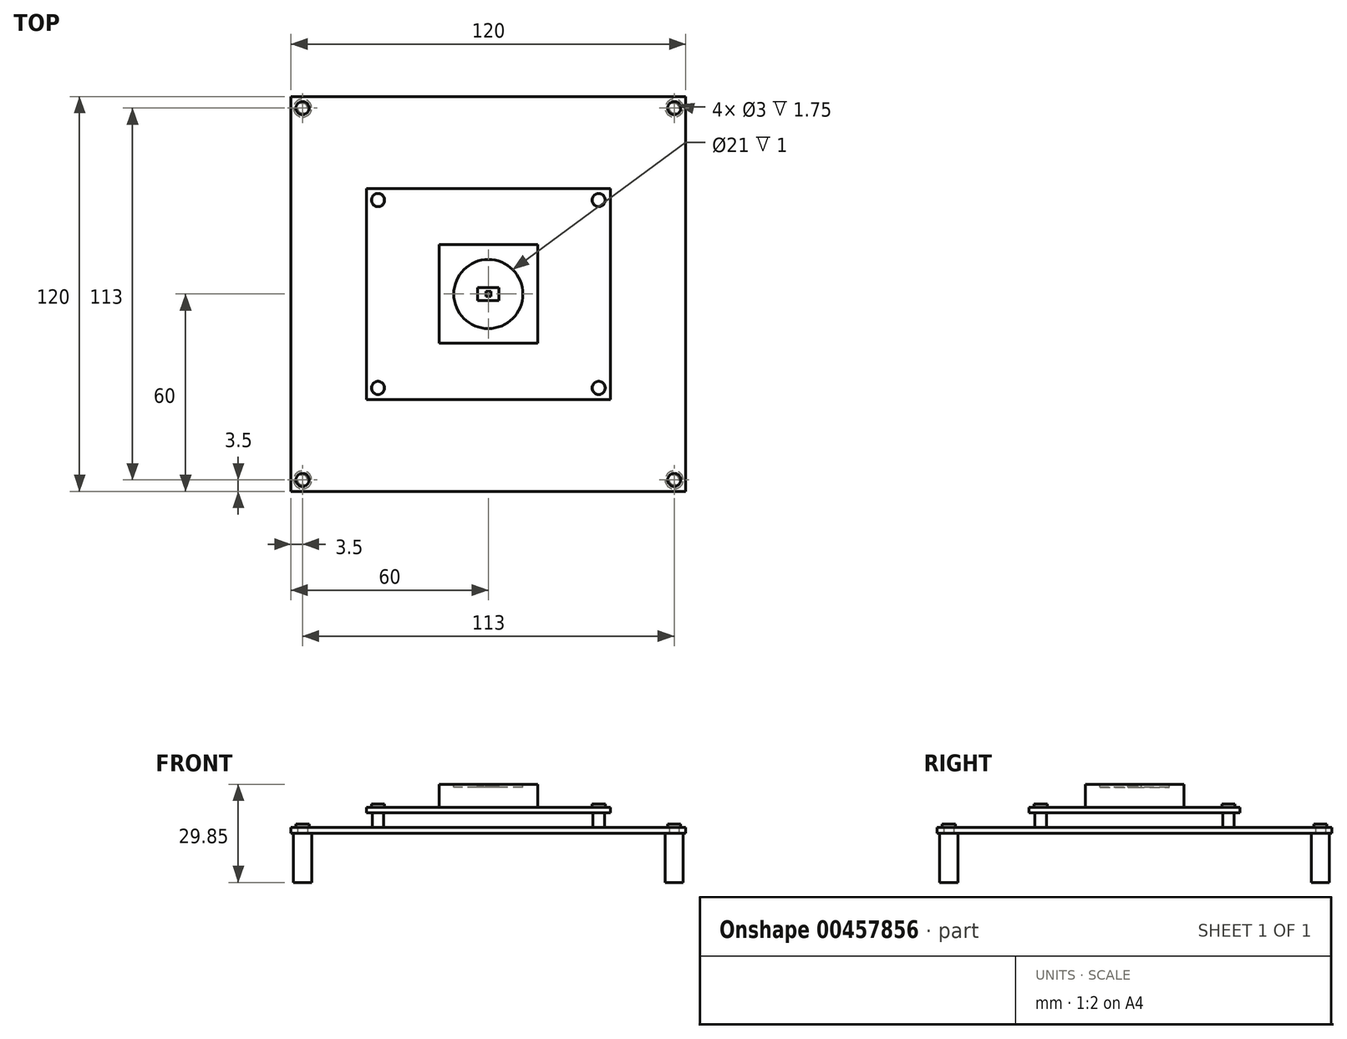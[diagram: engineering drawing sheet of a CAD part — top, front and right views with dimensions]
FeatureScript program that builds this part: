
annotation { "Feature Type Name" : "Feature", "Feature Type Description" : "" }
export const myFeature = defineFeature(function(context is Context, id is Id, definition is map)
    precondition{}
    {
        {
            var Q0;
            Q0=qCreatedBy(makeId("Top.planeOp"),FACE);
            var sketch = newSketch(context, id + "F0", { "sketchPlane" : qUnion([Q0])});
            skLineSegment(sketch, "E0.bottom", {"start": v(60, -60) * mm, "end": v(-60, -60) * mm});
            skLineSegment(sketch, "E0.top", {"start": v(60, 60) * mm, "end": v(-60, 60) * mm});
            skLineSegment(sketch, "E0.left", {"start": v(60, -60) * mm, "end": v(60, 60) * mm});
            skLineSegment(sketch, "E0.right", {"start": v(-60, -60) * mm, "end": v(-60, 60) * mm});
            skPoint(sketch, "E0.middle", {"position": v(0, 0) * mm});
            skCircle(sketch, "E1", {"center": v(-56.5, 56.5) * mm, "radius": 1.5 * mm});
            skCircle(sketch, "E2", {"center": v(56.5, 56.5) * mm, "radius": 1.5 * mm});
            skCircle(sketch, "E3", {"center": v(-56.5, -56.5) * mm, "radius": 1.5 * mm});
            skCircle(sketch, "E4", {"center": v(56.5, -56.5) * mm, "radius": 1.5 * mm});
            skCircle(sketch, "E5", {"center": v(-56.5, 56.5) * mm, "radius": 1.5 * mm, "construction": true});
            skCircle(sketch, "E6", {"center": v(-56.5, -56.5) * mm, "radius": 1.5 * mm, "construction": true});
            skCircle(sketch, "E7", {"center": v(56.5, -56.5) * mm, "radius": 1.5 * mm, "construction": true});
            skCircle(sketch, "E8", {"center": v(56.5, 56.5) * mm, "radius": 1.5 * mm, "construction": true});
            skCircle(sketch, "E9", {"center": v(-33.55, 28.55) * mm, "radius": 1.5 * mm, "construction": true});
            skCircle(sketch, "E10", {"center": v(33.55, 28.55) * mm, "radius": 1.5 * mm, "construction": true});
            skCircle(sketch, "E11", {"center": v(-33.55, -28.55) * mm, "radius": 1.5 * mm, "construction": true});
            skCircle(sketch, "E12", {"center": v(33.55, -28.55) * mm, "radius": 1.5 * mm, "construction": true});
            skLineSegment(sketch, "E13", {"start": v(-33.55, 28.55) * mm, "end": v(33.55, -28.55) * mm, "construction": true});
            skLineSegment(sketch, "E14", {"start": v(33.55, 28.55) * mm, "end": v(-33.55, -28.55) * mm, "construction": true});
            skLineSegment(sketch, "E15.bottom", {"start": v(37.05, 32.05) * mm, "end": v(-37.05, 32.05) * mm, "construction": true});
            skLineSegment(sketch, "E15.top", {"start": v(37.05, -32.05) * mm, "end": v(-37.05, -32.05) * mm, "construction": true});
            skLineSegment(sketch, "E15.left", {"start": v(37.05, 32.05) * mm, "end": v(37.05, -32.05) * mm, "construction": true});
            skLineSegment(sketch, "E15.right", {"start": v(-37.05, 32.05) * mm, "end": v(-37.05, -32.05) * mm, "construction": true});
            skLineSegment(sketch, "E16.bottom", {"start": v(15, -15) * mm, "end": v(-15, -15) * mm, "construction": true});
            skLineSegment(sketch, "E16.top", {"start": v(15, 15) * mm, "end": v(-15, 15) * mm, "construction": true});
            skLineSegment(sketch, "E16.left", {"start": v(15, -15) * mm, "end": v(15, 15) * mm, "construction": true});
            skLineSegment(sketch, "E16.right", {"start": v(-15, -15) * mm, "end": v(-15, 15) * mm, "construction": true});
            skSolve(sketch);
        }
        {
            var Q0;
            Q0=makeQuery(id+"F0.imprint","IMPRINT",FACE,{"disambiguationData":[TD([[makeQuery(id+"F0.imprint","IMPRINT",EDGE,{"derivedFrom":sQuery(id+"F0.wireOp",EDGE,"E0.bottom")}),-1.0]])]});
            extrude(context, id + "F1", {"entities" : qUnion([Q0]), "depth" : 1.75 * mm});
        }
        {
            var Q0;
            Q0=makeQuery(id+"F1.opExtrude","CAP_FACE",FACE,{"disambiguationData":[OSD([sQuery(id+"F0.wireOp",EDGE,"E0.bottom"),sQuery(id+"F0.wireOp",EDGE,"E0.top"),sQuery(id+"F0.wireOp",EDGE,"E0.left"),sQuery(id+"F0.wireOp",EDGE,"E0.right"),sQuery(id+"F0.wireOp",EDGE,"E1"),sQuery(id+"F0.wireOp",EDGE,"E2"),sQuery(id+"F0.wireOp",EDGE,"E3"),sQuery(id+"F0.wireOp",EDGE,"E4")])],"isStart":true});
            var sketch = newSketch(context, id + "F2", { "sketchPlane" : qUnion([Q0])});
            skCircle(sketch, "E17", {"center": v(56.5, -56.5) * mm, "radius": 2.75 * mm});
            skCircle(sketch, "E18", {"center": v(-56.5, -56.5) * mm, "radius": 2.75 * mm});
            skCircle(sketch, "E19", {"center": v(-56.5, 56.5) * mm, "radius": 2.75 * mm});
            skCircle(sketch, "E20", {"center": v(56.5, 56.5) * mm, "radius": 2.75 * mm});
            skSolve(sketch);
        }
        {
            var Q0;
            Q0=makeQuery(id+"F2.imprint","IMPRINT",FACE,{"disambiguationData":[TD([[makeQuery(id+"F2.imprint","IMPRINT",EDGE,{"derivedFrom":sQuery(id+"F2.wireOp",EDGE,"E19")}),1.0]])]});
            var Q1;
            Q1=makeQuery(id+"F2.imprint","IMPRINT",FACE,{"disambiguationData":[TD([[makeQuery(id+"F2.imprint","IMPRINT",EDGE,{"derivedFrom":makeQuery(id+"F1.opExtrude","CAP_EDGE",EDGE,{"disambiguationData":[OSD([sQuery(id+"F0.wireOp",EDGE,"E3")])],"isStart":true})}),-1.0]])]});
            var Q2;
            Q2=makeQuery(id+"F2.imprint","IMPRINT",FACE,{"disambiguationData":[TD([[makeQuery(id+"F2.imprint","IMPRINT",EDGE,{"derivedFrom":makeQuery(id+"F1.opExtrude","CAP_EDGE",EDGE,{"disambiguationData":[OSD([sQuery(id+"F0.wireOp",EDGE,"E4")])],"isStart":true})}),-1.0]])]});
            var Q3;
            Q3=makeQuery(id+"F2.imprint","IMPRINT",FACE,{"disambiguationData":[TD([[makeQuery(id+"F2.imprint","IMPRINT",EDGE,{"derivedFrom":sQuery(id+"F2.wireOp",EDGE,"E20")}),1.0]])]});
            var Q4;
            Q4=makeQuery(id+"F2.imprint","IMPRINT",FACE,{"disambiguationData":[TD([[makeQuery(id+"F2.imprint","IMPRINT",EDGE,{"derivedFrom":sQuery(id+"F2.wireOp",EDGE,"E17")}),1.0]])]});
            var Q5;
            Q5=makeQuery(id+"F2.imprint","IMPRINT",FACE,{"disambiguationData":[TD([[makeQuery(id+"F2.imprint","IMPRINT",EDGE,{"derivedFrom":makeQuery(id+"F1.opExtrude","CAP_EDGE",EDGE,{"disambiguationData":[OSD([sQuery(id+"F0.wireOp",EDGE,"E2")])],"isStart":true})}),-1.0]])]});
            var Q6;
            Q6=makeQuery(id+"F2.imprint","IMPRINT",FACE,{"disambiguationData":[TD([[makeQuery(id+"F2.imprint","IMPRINT",EDGE,{"derivedFrom":makeQuery(id+"F1.opExtrude","CAP_EDGE",EDGE,{"disambiguationData":[OSD([sQuery(id+"F0.wireOp",EDGE,"E1")])],"isStart":true})}),-1.0]])]});
            var Q7;
            Q7=makeQuery(id+"F2.imprint","IMPRINT",FACE,{"disambiguationData":[TD([[makeQuery(id+"F2.imprint","IMPRINT",EDGE,{"derivedFrom":sQuery(id+"F2.wireOp",EDGE,"E18")}),1.0]])]});
            extrude(context, id + "F3", {"entities" : qUnion([Q0, Q1, Q2, Q3, Q4, Q5, Q6, Q7]), "operationType" : NewBodyOperationType.ADD, "depth" : 15 * mm});
        }
        {
            var Q0;
            Q0=makeQuery(id+"F1.opExtrude","CAP_FACE",FACE,{"disambiguationData":[OSD([sQuery(id+"F0.wireOp",EDGE,"E0.bottom"),sQuery(id+"F0.wireOp",EDGE,"E0.top"),sQuery(id+"F0.wireOp",EDGE,"E0.left"),sQuery(id+"F0.wireOp",EDGE,"E0.right"),sQuery(id+"F0.wireOp",EDGE,"E1"),sQuery(id+"F0.wireOp",EDGE,"E2"),sQuery(id+"F0.wireOp",EDGE,"E3"),sQuery(id+"F0.wireOp",EDGE,"E4")])],"isStart":false});
            var sketch = newSketch(context, id + "F4", { "sketchPlane" : qUnion([Q0])});
            skCircle(sketch, "E21", {"center": v(-56.5, 56.5) * mm, "radius": 2 * mm});
            skCircle(sketch, "E22", {"center": v(56.5, 56.5) * mm, "radius": 2 * mm});
            skCircle(sketch, "E23", {"center": v(56.5, -56.5) * mm, "radius": 2 * mm});
            skCircle(sketch, "E24", {"center": v(-56.5, -56.5) * mm, "radius": 2 * mm});
            skPoint(sketch, "E25.0", {"position": v(-33.55, -28.55) * mm});
            skPoint(sketch, "E26.0", {"position": v(33.55, -28.55) * mm});
            skPoint(sketch, "E27.0", {"position": v(-33.55, 28.55) * mm});
            skPoint(sketch, "E28.0", {"position": v(33.55, 28.55) * mm});
            skCircle(sketch, "E29", {"center": v(-33.55, 28.55) * mm, "radius": 1.75 * mm});
            skCircle(sketch, "E30", {"center": v(33.55, 28.55) * mm, "radius": 1.75 * mm});
            skCircle(sketch, "E31", {"center": v(-33.55, -28.55) * mm, "radius": 1.75 * mm});
            skCircle(sketch, "E32", {"center": v(33.55, -28.55) * mm, "radius": 1.75 * mm});
            skSolve(sketch);
        }
        {
            var Q0;
            Q0=makeQuery(id+"F4.imprint","IMPRINT",FACE,{"disambiguationData":[TD([[makeQuery(id+"F4.imprint","IMPRINT",EDGE,{"derivedFrom":sQuery(id+"F4.wireOp",EDGE,"E21")}),1.0]])]});
            var Q1;
            Q1=makeQuery(id+"F4.imprint","IMPRINT",FACE,{"disambiguationData":[TD([[makeQuery(id+"F4.imprint","IMPRINT",EDGE,{"derivedFrom":makeQuery(id+"F1.opExtrude","CAP_EDGE",EDGE,{"disambiguationData":[OSD([sQuery(id+"F0.wireOp",EDGE,"E1")])],"isStart":false})}),1.0]])]});
            var Q2;
            Q2=makeQuery(id+"F4.imprint","IMPRINT",FACE,{"disambiguationData":[TD([[makeQuery(id+"F4.imprint","IMPRINT",EDGE,{"derivedFrom":sQuery(id+"F4.wireOp",EDGE,"E22")}),1.0]])]});
            var Q3;
            Q3=makeQuery(id+"F4.imprint","IMPRINT",FACE,{"disambiguationData":[TD([[makeQuery(id+"F4.imprint","IMPRINT",EDGE,{"derivedFrom":makeQuery(id+"F1.opExtrude","CAP_EDGE",EDGE,{"disambiguationData":[OSD([sQuery(id+"F0.wireOp",EDGE,"E2")])],"isStart":false})}),1.0]])]});
            var Q4;
            Q4=makeQuery(id+"F4.imprint","IMPRINT",FACE,{"disambiguationData":[TD([[makeQuery(id+"F4.imprint","IMPRINT",EDGE,{"derivedFrom":sQuery(id+"F4.wireOp",EDGE,"E23")}),1.0]])]});
            var Q5;
            Q5=makeQuery(id+"F4.imprint","IMPRINT",FACE,{"disambiguationData":[TD([[makeQuery(id+"F4.imprint","IMPRINT",EDGE,{"derivedFrom":makeQuery(id+"F1.opExtrude","CAP_EDGE",EDGE,{"disambiguationData":[OSD([sQuery(id+"F0.wireOp",EDGE,"E4")])],"isStart":false})}),1.0]])]});
            var Q6;
            Q6=makeQuery(id+"F4.imprint","IMPRINT",FACE,{"disambiguationData":[TD([[makeQuery(id+"F4.imprint","IMPRINT",EDGE,{"derivedFrom":sQuery(id+"F4.wireOp",EDGE,"E24")}),1.0]])]});
            var Q7;
            Q7=makeQuery(id+"F4.imprint","IMPRINT",FACE,{"disambiguationData":[TD([[makeQuery(id+"F4.imprint","IMPRINT",EDGE,{"derivedFrom":makeQuery(id+"F1.opExtrude","CAP_EDGE",EDGE,{"disambiguationData":[OSD([sQuery(id+"F0.wireOp",EDGE,"E3")])],"isStart":false})}),1.0]])]});
            extrude(context, id + "F5", {"entities" : qUnion([Q0, Q1, Q2, Q3, Q4, Q5, Q6, Q7]), "operationType" : NewBodyOperationType.ADD, "depth" : 1 * mm});
        }
        {
            var Q0;
            Q0=makeQuery(id+"F4.imprint","IMPRINT",FACE,{"disambiguationData":[TD([[makeQuery(id+"F4.imprint","IMPRINT",EDGE,{"derivedFrom":sQuery(id+"F4.wireOp",EDGE,"E31")}),1.0]])]});
            var Q1;
            Q1=makeQuery(id+"F4.imprint","IMPRINT",FACE,{"disambiguationData":[TD([[makeQuery(id+"F4.imprint","IMPRINT",EDGE,{"derivedFrom":sQuery(id+"F4.wireOp",EDGE,"E32")}),1.0]])]});
            var Q2;
            Q2=makeQuery(id+"F4.imprint","IMPRINT",FACE,{"disambiguationData":[TD([[makeQuery(id+"F4.imprint","IMPRINT",EDGE,{"derivedFrom":sQuery(id+"F4.wireOp",EDGE,"E30")}),1.0]])]});
            var Q3;
            Q3=makeQuery(id+"F4.imprint","IMPRINT",FACE,{"disambiguationData":[TD([[makeQuery(id+"F4.imprint","IMPRINT",EDGE,{"derivedFrom":sQuery(id+"F4.wireOp",EDGE,"E29")}),1.0]])]});
            extrude(context, id + "F6", {"entities" : qUnion([Q0, Q1, Q2, Q3]), "operationType" : NewBodyOperationType.ADD, "depth" : 4.35 * mm});
        }
        {
            var Q0;
            Q0=makeQuery(id+"F6.opExtrude","CAP_FACE",FACE,{"disambiguationData":[OSD([sQuery(id+"F4.wireOp",EDGE,"E29")])],"isStart":false});
            var sketch = newSketch(context, id + "F7", { "sketchPlane" : qUnion([Q0])});
            skPoint(sketch, "E33.0", {"position": v(-37.05, 32.05) * mm});
            skPoint(sketch, "E34.0", {"position": v(37.05, -32.05) * mm});
            skLineSegment(sketch, "E35.bottom", {"start": v(-37.05, 32.05) * mm, "end": v(37.05, 32.05) * mm});
            skLineSegment(sketch, "E35.top", {"start": v(-37.05, -32.05) * mm, "end": v(37.05, -32.05) * mm});
            skLineSegment(sketch, "E35.left", {"start": v(-37.05, 32.05) * mm, "end": v(-37.05, -32.05) * mm});
            skLineSegment(sketch, "E35.right", {"start": v(37.05, 32.05) * mm, "end": v(37.05, -32.05) * mm});
            skSolve(sketch);
        }
        {
            var Q0;
            Q0 = qSketchRegion(id + "F7", true);
            extrude(context, id + "F8", {"entities" : qUnion([Q0]), "operationType" : NewBodyOperationType.ADD, "depth" : 1.75 * mm});
        }
        {
            var Q0;
            Q0=makeQuery(id+"F8.opExtrude","CAP_FACE",FACE,{"disambiguationData":[OSD([sQuery(id+"F7.wireOp",EDGE,"E35.bottom"),sQuery(id+"F7.wireOp",EDGE,"E35.top"),sQuery(id+"F7.wireOp",EDGE,"E35.left"),sQuery(id+"F7.wireOp",EDGE,"E35.right")])],"isStart":false});
            var sketch = newSketch(context, id + "F9", { "sketchPlane" : qUnion([Q0])});
            skPoint(sketch, "E36.0", {"position": v(-33.55, 28.55) * mm});
            skPoint(sketch, "E37.0", {"position": v(33.55, 28.55) * mm});
            skPoint(sketch, "E38.0", {"position": v(33.55, -28.55) * mm});
            skPoint(sketch, "E39.0", {"position": v(-33.55, -28.55) * mm});
            skPoint(sketch, "E40.0", {"position": v(-15, 15) * mm});
            skPoint(sketch, "E41.0", {"position": v(15, 15) * mm});
            skPoint(sketch, "E42.0", {"position": v(15, -15) * mm});
            skPoint(sketch, "E43.0", {"position": v(-15, -15) * mm});
            skLineSegment(sketch, "E44.bottom", {"start": v(-15, 15) * mm, "end": v(15, 15) * mm});
            skLineSegment(sketch, "E44.top", {"start": v(-15, -15) * mm, "end": v(15, -15) * mm});
            skLineSegment(sketch, "E44.left", {"start": v(-15, 15) * mm, "end": v(-15, -15) * mm});
            skLineSegment(sketch, "E44.right", {"start": v(15, 15) * mm, "end": v(15, -15) * mm});
            skCircle(sketch, "E45", {"center": v(-33.55, 28.55) * mm, "radius": 2 * mm});
            skCircle(sketch, "E46", {"center": v(33.55, 28.55) * mm, "radius": 2 * mm});
            skCircle(sketch, "E47", {"center": v(33.55, -28.55) * mm, "radius": 2 * mm});
            skCircle(sketch, "E48", {"center": v(-33.55, -28.55) * mm, "radius": 2 * mm});
            skSolve(sketch);
        }
        {
            var Q0;
            Q0=makeQuery(id+"F9.imprint","IMPRINT",FACE,{"disambiguationData":[TD([[makeQuery(id+"F9.imprint","IMPRINT",EDGE,{"derivedFrom":sQuery(id+"F9.wireOp",EDGE,"E46")}),1.0]])]});
            var Q1;
            Q1=makeQuery(id+"F9.imprint","IMPRINT",FACE,{"disambiguationData":[TD([[makeQuery(id+"F9.imprint","IMPRINT",EDGE,{"derivedFrom":sQuery(id+"F9.wireOp",EDGE,"E45")}),1.0]])]});
            var Q2;
            Q2=makeQuery(id+"F9.imprint","IMPRINT",FACE,{"disambiguationData":[TD([[makeQuery(id+"F9.imprint","IMPRINT",EDGE,{"derivedFrom":sQuery(id+"F9.wireOp",EDGE,"E47")}),1.0]])]});
            var Q3;
            Q3=makeQuery(id+"F9.imprint","IMPRINT",FACE,{"disambiguationData":[TD([[makeQuery(id+"F9.imprint","IMPRINT",EDGE,{"derivedFrom":sQuery(id+"F9.wireOp",EDGE,"E48")}),1.0]])]});
            extrude(context, id + "F10", {"entities" : qUnion([Q0, Q1, Q2, Q3]), "operationType" : NewBodyOperationType.ADD, "depth" : 1 * mm});
        }
        {
            var Q0;
            Q0=makeQuery(id+"F9.imprint","IMPRINT",FACE,{"disambiguationData":[TD([[makeQuery(id+"F9.imprint","IMPRINT",EDGE,{"derivedFrom":sQuery(id+"F9.wireOp",EDGE,"E44.bottom")}),-1.0]])]});
            extrude(context, id + "F11", {"entities" : qUnion([Q0]), "operationType" : NewBodyOperationType.ADD, "depth" : 7 * mm});
        }
        {
            var Q0;
            Q0=makeQuery(id+"F11.opExtrude","CAP_FACE",FACE,{"disambiguationData":[OSD([sQuery(id+"F9.wireOp",EDGE,"E44.bottom"),sQuery(id+"F9.wireOp",EDGE,"E44.top"),sQuery(id+"F9.wireOp",EDGE,"E44.left"),sQuery(id+"F9.wireOp",EDGE,"E44.right")])],"isStart":false});
            var sketch = newSketch(context, id + "F12", { "sketchPlane" : qUnion([Q0])});
            skCircle(sketch, "E49", {"center": v(0, 0) * mm, "radius": 10.5 * mm});
            skLineSegment(sketch, "E50.bottom", {"start": v(0.75, 0.75) * mm, "end": v(-0.75, 0.75) * mm});
            skLineSegment(sketch, "E50.top", {"start": v(0.75, -0.75) * mm, "end": v(-0.75, -0.75) * mm});
            skLineSegment(sketch, "E50.left", {"start": v(0.75, 0.75) * mm, "end": v(0.75, -0.75) * mm});
            skLineSegment(sketch, "E50.right", {"start": v(-0.75, 0.75) * mm, "end": v(-0.75, -0.75) * mm});
            skLineSegment(sketch, "E51.bottom", {"start": v(3.25, -2) * mm, "end": v(-3.25, -2) * mm});
            skLineSegment(sketch, "E51.top", {"start": v(3.25, 2) * mm, "end": v(-3.25, 2) * mm});
            skLineSegment(sketch, "E51.left", {"start": v(3.25, -2) * mm, "end": v(3.25, 2) * mm});
            skLineSegment(sketch, "E51.right", {"start": v(-3.25, -2) * mm, "end": v(-3.25, 2) * mm});
            skSolve(sketch);
        }
        {
            var Q0;
            Q0=makeQuery(id+"F12.imprint","IMPRINT",FACE,{"disambiguationData":[TD([[makeQuery(id+"F12.imprint","IMPRINT",EDGE,{"derivedFrom":sQuery(id+"F12.wireOp",EDGE,"E49")}),1.0]])]});
            extrude(context, id + "F13", {"entities" : qUnion([Q0]), "operationType" : NewBodyOperationType.REMOVE, "oppositeDirection" : true, "depth" : 1 * mm});
        }
        {
            var Q0;
            Q0=makeQuery(id+"F12.imprint","IMPRINT",FACE,{"disambiguationData":[TD([[makeQuery(id+"F12.imprint","IMPRINT",EDGE,{"derivedFrom":sQuery(id+"F12.wireOp",EDGE,"E50.bottom")}),1.0]])]});
            extrude(context, id + "F14", {"entities" : qUnion([Q0]), "operationType" : NewBodyOperationType.REMOVE, "oppositeDirection" : true, "depth" : 0.3 * mm});
        }
        {
            var Q0;
            Q0=makeQuery(id+"F12.imprint","IMPRINT",FACE,{"disambiguationData":[TD([[makeQuery(id+"F12.imprint","IMPRINT",EDGE,{"derivedFrom":sQuery(id+"F12.wireOp",EDGE,"E50.bottom")}),-1.0]])]});
            extrude(context, id + "F15", {"entities" : qUnion([Q0]), "operationType" : NewBodyOperationType.REMOVE, "oppositeDirection" : true, "depth" : 0.5 * mm});
        }
    });
